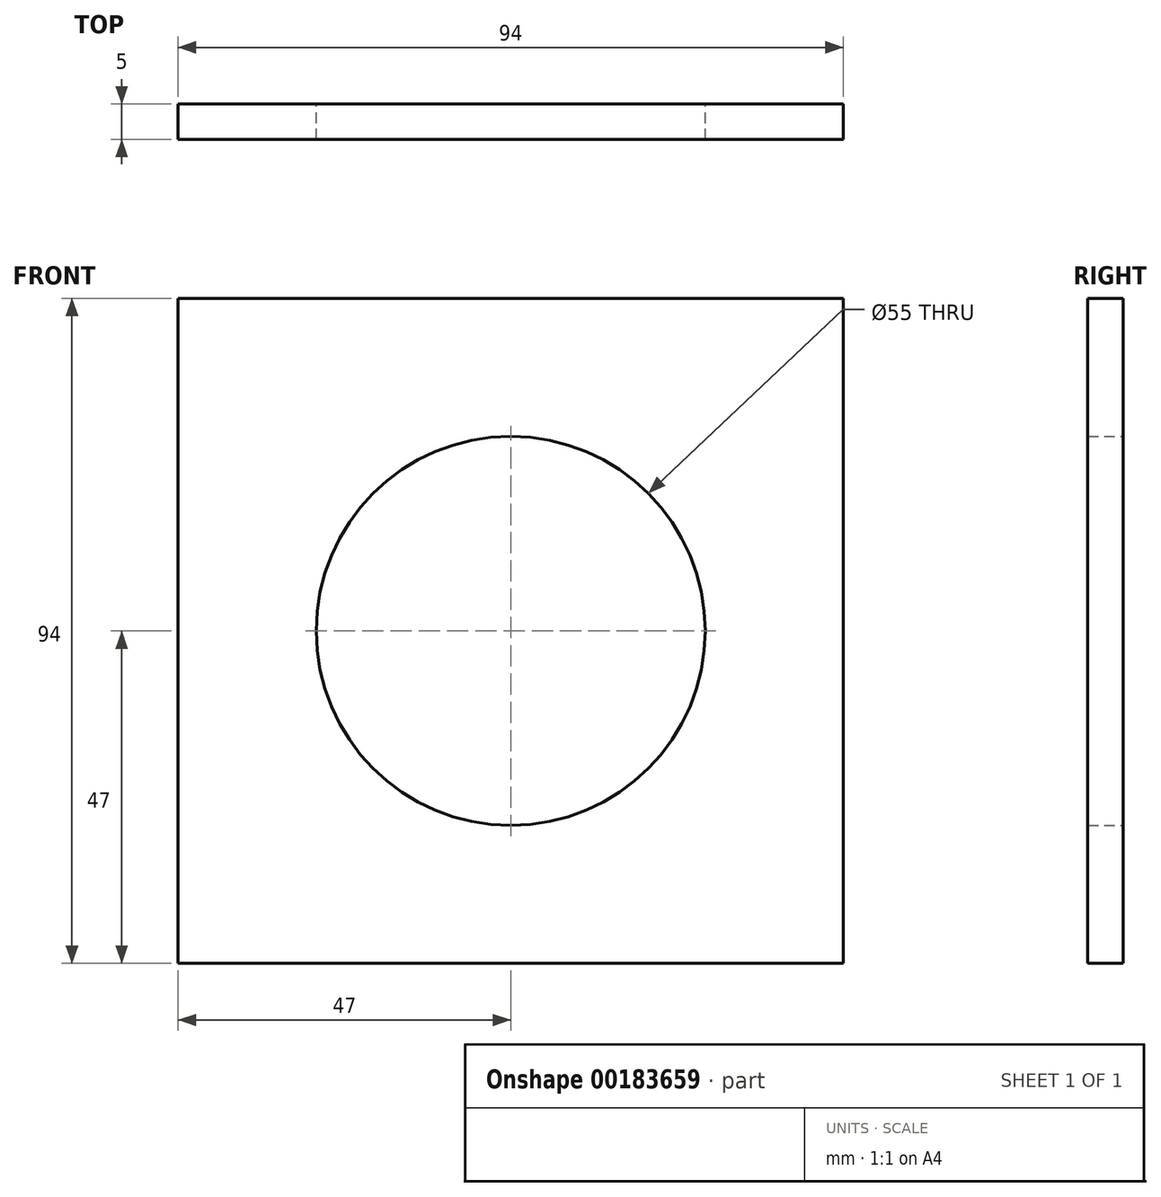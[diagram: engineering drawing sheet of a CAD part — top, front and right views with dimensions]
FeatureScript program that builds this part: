
annotation { "Feature Type Name" : "Feature", "Feature Type Description" : "" }
export const myFeature = defineFeature(function(context is Context, id is Id, definition is map)
    precondition{}
    {
        {
            var Q0;
            Q0=qCreatedBy(makeId("Front.planeOp"),FACE);
            var sketch = newSketch(context, id + "F0", { "sketchPlane" : qUnion([Q0])});
            skLineSegment(sketch, "E0.bottom", {"start": v(47, -47) * mm, "end": v(-47, -47) * mm});
            skLineSegment(sketch, "E0.top", {"start": v(47, 47) * mm, "end": v(-47, 47) * mm});
            skLineSegment(sketch, "E0.left", {"start": v(47, -47) * mm, "end": v(47, 47) * mm});
            skLineSegment(sketch, "E0.right", {"start": v(-47, -47) * mm, "end": v(-47, 47) * mm});
            skPoint(sketch, "E0.middle", {"position": v(0, 0) * mm});
            skCircle(sketch, "E1", {"center": v(0, 0) * mm, "radius": 27.5 * mm});
            skSolve(sketch);
        }
        {
            var Q0;
            Q0=makeQuery(id+"F0.imprint","IMPRINT",FACE,{"disambiguationData":[TD([[makeQuery(id+"F0.imprint","IMPRINT",EDGE,{"derivedFrom":sQuery(id+"F0.wireOp",EDGE,"E0.bottom")}),-1.0]])]});
            extrude(context, id + "F1", {"entities" : qUnion([Q0]), "depth" : 5 * mm});
        }
    });
